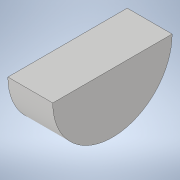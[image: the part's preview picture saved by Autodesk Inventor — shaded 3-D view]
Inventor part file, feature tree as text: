
AUTODESK INVENTOR PART (.ipt)
format: ipt  version: 2021 (Build 250183000, 183)  size: 87,040 bytes
history: native  units: in
note: dims shown in document units (in); Inventor stores cm internally (conversion verified against a paired STEP export)
features: extrude x1, sketch x1
ambient origin geometry x8: Origin, YZ Plane, XZ Plane, XY Plane, X Axis, Y Axis, Z Axis, Center Point
bodies: Solid1 (feature_tree)
feature tree (2):
  extrude  "Extrusion1"  Depth=0.188in TaperAngle=0.0deg
  sketch  "Sketch1"  dims[d0=0.5in d1=0.188in d2=0.0in]
